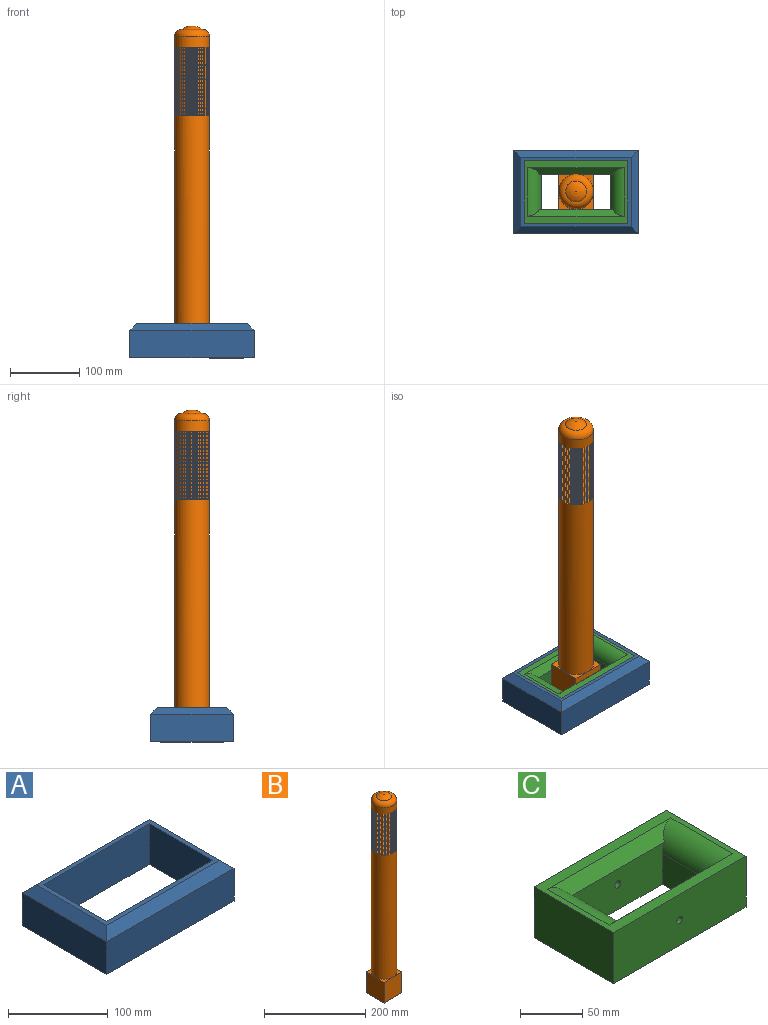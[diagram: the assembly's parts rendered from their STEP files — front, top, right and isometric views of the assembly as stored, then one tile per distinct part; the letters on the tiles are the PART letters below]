
ASSEMBLY  parts=3 mates=2
PART A: 14 faces, bbox 180x120x50 mm
  f0: plane 150x50mm, normal (0,-1,0), area 7500mm2, adj f1,f7,f8,f13
  f1: plane 90x50mm, normal (-1,0,0), area 4500mm2, adj f0,f2,f8,f13
  f2: plane 150x50mm, normal (0,1,0), area 7500mm2, adj f1,f7,f8,f13
  f3: plane 120x40mm, normal (1,0,0), area 4800mm2, adj f4,f6,f10,f13
  f4: plane 180x40mm, normal (0,1,0), area 7200mm2, adj f3,f5,f9,f13
  f5: plane 120x40mm, normal (-1,0,0), area 4800mm2, adj f4,f6,f11,f13
  f6: plane 180x40mm, normal (0,-1,0), area 7200mm2, adj f3,f5,f12,f13
  f7: plane 90x50mm, normal (1,0,0), area 4500mm2, adj f0,f2,f8,f13
  f8: plane 160x100mm, normal (0,0,1), area 2500mm2, adj f0,f1,f2,f7,f9,f10,f11,f12
  f9: plane 180x10mm, normal (0,0.71,0.71), area 2404.2mm2, adj f4,f8,f10,f11
  f10: plane 120x10mm, normal (0.71,0,0.71), area 1555.6mm2, adj f3,f8,f9,f12
  f11: plane 120x10mm, normal (-0.71,0,0.71), area 1555.6mm2, adj f5,f8,f9,f12
  f12: plane 180x10mm, normal (0,-0.71,0.71), area 2404.2mm2, adj f6,f8,f10,f11
  f13: plane 180x120mm, normal (0,0,-1), area 8100mm2, adj f0,f1,f2,f3,f4,f5,f6,f7
PART B: 213 faces, bbox 54.1x54.1x480 mm
  f0: cylinder r=25mm len=300mm, axis (0,0,-1), area 47123.9mm2, adj f1,f204,f205,f206,f212
  f1: plane 50x50mm, normal (0,0,1), area 373.1mm2, adj f0,f2
  f2: cylinder r=22.5mm len=45mm, axis (0,0,-1), area 141.4mm2, adj f1,f5
  f3: cylinder r=25mm len=50mm, axis (0,0,-1), area 157.1mm2, adj f4,f5
  f4: plane 50x50mm, normal (0,0,1), area 373.1mm2, adj f3,f10
  f5: plane 50x50mm, normal (0,0,-1), area 373.1mm2, adj f2,f3
  f6: cylinder r=22.5mm len=45mm, axis (0,0,-1), area 141.4mm2, adj f9,f12
  f7: cylinder r=25mm len=50mm, axis (0,0,-1), area 157.1mm2, adj f8,f9
  f8: plane 50x50mm, normal (0,0,1), area 373.1mm2, adj f7,f14
  f9: plane 50x50mm, normal (0,0,-1), area 373.1mm2, adj f6,f7
  f10: cylinder r=22.5mm len=45mm, axis (0,0,-1), area 141.4mm2, adj f4,f13
  f11: cylinder r=25mm len=50mm, axis (0,0,-1), area 157.1mm2, adj f12,f13
  f12: plane 50x50mm, normal (0,0,1), area 373.1mm2, adj f6,f11
  f13: plane 50x50mm, normal (0,0,-1), area 373.1mm2, adj f10,f11
  f14: cylinder r=22.5mm len=45mm, axis (0,0,-1), area 141.4mm2, adj f8,f17
  f15: cylinder r=25mm len=50mm, axis (0,0,-1), area 157.1mm2, adj f16,f17
  f16: plane 50x50mm, normal (0,0,1), area 373.1mm2, adj f15,f18
  f17: plane 50x50mm, normal (0,0,-1), area 373.1mm2, adj f14,f15
  f18: cylinder r=22.5mm len=45mm, axis (0,0,-1), area 141.4mm2, adj f16,f21
  f19: cylinder r=25mm len=50mm, axis (0,0,-1), area 157.1mm2, adj f20,f21
  f20: plane 50x50mm, normal (0,0,1), area 373.1mm2, adj f19,f22
  f21: plane 50x50mm, normal (0,0,-1), area 373.1mm2, adj f18,f19
  f22: cylinder r=22.5mm len=45mm, axis (0,0,-1), area 141.4mm2, adj f20,f25
  f23: cylinder r=25mm len=50mm, axis (0,0,-1), area 157.1mm2, adj f24,f25
  f24: plane 50x50mm, normal (0,0,1), area 373.1mm2, adj f23,f26
  f25: plane 50x50mm, normal (0,0,-1), area 373.1mm2, adj f22,f23
  f26: cylinder r=22.5mm len=45mm, axis (0,0,-1), area 141.4mm2, adj f24,f29
  f27: cylinder r=25mm len=50mm, axis (0,0,-1), area 157.1mm2, adj f28,f29
  f28: plane 50x50mm, normal (0,0,1), area 373.1mm2, adj f27,f30
  f29: plane 50x50mm, normal (0,0,-1), area 373.1mm2, adj f26,f27
  f30: cylinder r=22.5mm len=45mm, axis (0,0,-1), area 141.4mm2, adj f28,f33
  f31: cylinder r=25mm len=50mm, axis (0,0,-1), area 157.1mm2, adj f32,f33
  f32: plane 50x50mm, normal (0,0,1), area 373.1mm2, adj f31,f34
  f33: plane 50x50mm, normal (0,0,-1), area 373.1mm2, adj f30,f31
  f34: cylinder r=22.5mm len=45mm, axis (0,0,-1), area 141.4mm2, adj f32,f37
  f35: cylinder r=25mm len=50mm, axis (0,0,-1), area 157.1mm2, adj f36,f37
  f36: plane 50x50mm, normal (0,0,1), area 373.1mm2, adj f35,f38
  f37: plane 50x50mm, normal (0,0,-1), area 373.1mm2, adj f34,f35
  f38: cylinder r=22.5mm len=45mm, axis (0,0,-1), area 141.4mm2, adj f36,f41
  f39: cylinder r=25mm len=50mm, axis (0,0,-1), area 157.1mm2, adj f40,f41
  f40: plane 50x50mm, normal (0,0,1), area 373.1mm2, adj f39,f42
  f41: plane 50x50mm, normal (0,0,-1), area 373.1mm2, adj f38,f39
  f42: cylinder r=22.5mm len=45mm, axis (0,0,-1), area 141.4mm2, adj f40,f45
  f43: cylinder r=25mm len=50mm, axis (0,0,-1), area 157.1mm2, adj f44,f45
  f44: plane 50x50mm, normal (0,0,1), area 373.1mm2, adj f43,f46
  f45: plane 50x50mm, normal (0,0,-1), area 373.1mm2, adj f42,f43
  f46: cylinder r=22.5mm len=45mm, axis (0,0,-1), area 141.4mm2, adj f44,f49
  f47: cylinder r=25mm len=50mm, axis (0,0,-1), area 157.1mm2, adj f48,f49
  f48: plane 50x50mm, normal (0,0,1), area 373.1mm2, adj f47,f50
  f49: plane 50x50mm, normal (0,0,-1), area 373.1mm2, adj f46,f47
  f50: cylinder r=22.5mm len=45mm, axis (0,0,-1), area 141.4mm2, adj f48,f53
  f51: cylinder r=25mm len=50mm, axis (0,0,-1), area 157.1mm2, adj f52,f53
  f52: plane 50x50mm, normal (0,0,1), area 373.1mm2, adj f51,f54
  f53: plane 50x50mm, normal (0,0,-1), area 373.1mm2, adj f50,f51
  f54: cylinder r=22.5mm len=45mm, axis (0,0,-1), area 141.4mm2, adj f52,f57
  f55: cylinder r=25mm len=50mm, axis (0,0,-1), area 157.1mm2, adj f56,f57
  f56: plane 50x50mm, normal (0,0,1), area 373.1mm2, adj f55,f58
  f57: plane 50x50mm, normal (0,0,-1), area 373.1mm2, adj f54,f55
  f58: cylinder r=22.5mm len=45mm, axis (0,0,-1), area 141.4mm2, adj f56,f61
  f59: cylinder r=25mm len=50mm, axis (0,0,-1), area 157.1mm2, adj f60,f61
  f60: plane 50x50mm, normal (0,0,1), area 373.1mm2, adj f59,f62
  f61: plane 50x50mm, normal (0,0,-1), area 373.1mm2, adj f58,f59
  f62: cylinder r=22.5mm len=45mm, axis (0,0,-1), area 141.4mm2, adj f60,f65
  f63: cylinder r=25mm len=50mm, axis (0,0,-1), area 157.1mm2, adj f64,f65
  f64: plane 50x50mm, normal (0,0,1), area 373.1mm2, adj f63,f66
  f65: plane 50x50mm, normal (0,0,-1), area 373.1mm2, adj f62,f63
  f66: cylinder r=22.5mm len=45mm, axis (0,0,-1), area 141.4mm2, adj f64,f69
  f67: cylinder r=25mm len=50mm, axis (0,0,-1), area 157.1mm2, adj f68,f69
  f68: plane 50x50mm, normal (0,0,1), area 373.1mm2, adj f67,f70
  f69: plane 50x50mm, normal (0,0,-1), area 373.1mm2, adj f66,f67
  f70: cylinder r=22.5mm len=45mm, axis (0,0,-1), area 141.4mm2, adj f68,f73
  f71: cylinder r=25mm len=50mm, axis (0,0,-1), area 157.1mm2, adj f72,f73
  f72: plane 50x50mm, normal (0,0,1), area 373.1mm2, adj f71,f74
  f73: plane 50x50mm, normal (0,0,-1), area 373.1mm2, adj f70,f71
  f74: cylinder r=22.5mm len=45mm, axis (0,0,-1), area 141.4mm2, adj f72,f77
  f75: cylinder r=25mm len=50mm, axis (0,0,-1), area 157.1mm2, adj f76,f77
  f76: plane 50x50mm, normal (0,0,1), area 373.1mm2, adj f75,f78
  f77: plane 50x50mm, normal (0,0,-1), area 373.1mm2, adj f74,f75
  f78: cylinder r=22.5mm len=45mm, axis (0,0,-1), area 141.4mm2, adj f76,f81
  f79: cylinder r=25mm len=50mm, axis (0,0,-1), area 157.1mm2, adj f80,f81
  f80: plane 50x50mm, normal (0,0,1), area 373.1mm2, adj f79,f82
  f81: plane 50x50mm, normal (0,0,-1), area 373.1mm2, adj f78,f79
  f82: cylinder r=22.5mm len=45mm, axis (0,0,-1), area 141.4mm2, adj f80,f85
  f83: cylinder r=25mm len=50mm, axis (0,0,-1), area 157.1mm2, adj f84,f85
  f84: plane 50x50mm, normal (0,0,1), area 373.1mm2, adj f83,f86
  f85: plane 50x50mm, normal (0,0,-1), area 373.1mm2, adj f82,f83
  f86: cylinder r=22.5mm len=45mm, axis (0,0,-1), area 141.4mm2, adj f84,f89
  f87: cylinder r=25mm len=50mm, axis (0,0,-1), area 157.1mm2, adj f88,f89
  f88: plane 50x50mm, normal (0,0,1), area 373.1mm2, adj f87,f90
  f89: plane 50x50mm, normal (0,0,-1), area 373.1mm2, adj f86,f87
  f90: cylinder r=22.5mm len=45mm, axis (0,0,-1), area 141.4mm2, adj f88,f93
  f91: cylinder r=25mm len=50mm, axis (0,0,-1), area 157.1mm2, adj f92,f93
  f92: plane 50x50mm, normal (0,0,1), area 373.1mm2, adj f91,f94
  f93: plane 50x50mm, normal (0,0,-1), area 373.1mm2, adj f90,f91
  f94: cylinder r=22.5mm len=45mm, axis (0,0,-1), area 141.4mm2, adj f92,f97
  f95: cylinder r=25mm len=50mm, axis (0,0,-1), area 157.1mm2, adj f96,f97
  f96: plane 50x50mm, normal (0,0,1), area 373.1mm2, adj f95,f98
  f97: plane 50x50mm, normal (0,0,-1), area 373.1mm2, adj f94,f95
  f98: cylinder r=22.5mm len=45mm, axis (0,0,-1), area 141.4mm2, adj f96,f101
  f99: cylinder r=25mm len=50mm, axis (0,0,-1), area 157.1mm2, adj f100,f101
  f100: plane 50x50mm, normal (0,0,1), area 373.1mm2, adj f99,f102
  f101: plane 50x50mm, normal (0,0,-1), area 373.1mm2, adj f98,f99
  f102: cylinder r=22.5mm len=45mm, axis (0,0,-1), area 141.4mm2, adj f100,f105
  f103: cylinder r=25mm len=50mm, axis (0,0,-1), area 157.1mm2, adj f104,f105
  f104: plane 50x50mm, normal (0,0,1), area 373.1mm2, adj f103,f106
  f105: plane 50x50mm, normal (0,0,-1), area 373.1mm2, adj f102,f103
  f106: cylinder r=22.5mm len=45mm, axis (0,0,-1), area 141.4mm2, adj f104,f109
  f107: cylinder r=25mm len=50mm, axis (0,0,-1), area 157.1mm2, adj f108,f109
  f108: plane 50x50mm, normal (0,0,1), area 373.1mm2, adj f107,f110
  f109: plane 50x50mm, normal (0,0,-1), area 373.1mm2, adj f106,f107
  f110: cylinder r=22.5mm len=45mm, axis (0,0,-1), area 141.4mm2, adj f108,f113
  f111: cylinder r=25mm len=50mm, axis (0,0,-1), area 157.1mm2, adj f112,f113
  f112: plane 50x50mm, normal (0,0,1), area 373.1mm2, adj f111,f114
  f113: plane 50x50mm, normal (0,0,-1), area 373.1mm2, adj f110,f111
  f114: cylinder r=22.5mm len=45mm, axis (0,0,-1), area 141.4mm2, adj f112,f117
  f115: cylinder r=25mm len=50mm, axis (0,0,-1), area 157.1mm2, adj f116,f117
  f116: plane 50x50mm, normal (0,0,1), area 373.1mm2, adj f115,f118
  f117: plane 50x50mm, normal (0,0,-1), area 373.1mm2, adj f114,f115
  f118: cylinder r=22.5mm len=45mm, axis (0,0,-1), area 141.4mm2, adj f116,f121
  f119: cylinder r=25mm len=50mm, axis (0,0,-1), area 157.1mm2, adj f120,f121
  f120: plane 50x50mm, normal (0,0,1), area 373.1mm2, adj f119,f122
  f121: plane 50x50mm, normal (0,0,-1), area 373.1mm2, adj f118,f119
  f122: cylinder r=22.5mm len=45mm, axis (0,0,-1), area 141.4mm2, adj f120,f125
  f123: cylinder r=25mm len=50mm, axis (0,0,-1), area 157.1mm2, adj f124,f125
  f124: plane 50x50mm, normal (0,0,1), area 373.1mm2, adj f123,f126
  f125: plane 50x50mm, normal (0,0,-1), area 373.1mm2, adj f122,f123
  f126: cylinder r=22.5mm len=45mm, axis (0,0,-1), area 141.4mm2, adj f124,f129
  f127: cylinder r=25mm len=50mm, axis (0,0,-1), area 157.1mm2, adj f128,f129
  f128: plane 50x50mm, normal (0,0,1), area 373.1mm2, adj f127,f130
  f129: plane 50x50mm, normal (0,0,-1), area 373.1mm2, adj f126,f127
  f130: cylinder r=22.5mm len=45mm, axis (0,0,-1), area 141.4mm2, adj f128,f133
  f131: cylinder r=25mm len=50mm, axis (0,0,-1), area 157.1mm2, adj f132,f133
  f132: plane 50x50mm, normal (0,0,1), area 373.1mm2, adj f131,f134
  f133: plane 50x50mm, normal (0,0,-1), area 373.1mm2, adj f130,f131
  f134: cylinder r=22.5mm len=45mm, axis (0,0,-1), area 141.4mm2, adj f132,f137
  f135: cylinder r=25mm len=50mm, axis (0,0,-1), area 157.1mm2, adj f136,f137
  f136: plane 50x50mm, normal (0,0,1), area 373.1mm2, adj f135,f138
  f137: plane 50x50mm, normal (0,0,-1), area 373.1mm2, adj f134,f135
  f138: cylinder r=22.5mm len=45mm, axis (0,0,-1), area 141.4mm2, adj f136,f141
  f139: cylinder r=25mm len=50mm, axis (0,0,-1), area 157.1mm2, adj f140,f141
  f140: plane 50x50mm, normal (0,0,1), area 373.1mm2, adj f139,f142
  f141: plane 50x50mm, normal (0,0,-1), area 373.1mm2, adj f138,f139
  f142: cylinder r=22.5mm len=45mm, axis (0,0,-1), area 141.4mm2, adj f140,f145
  f143: cylinder r=25mm len=50mm, axis (0,0,-1), area 157.1mm2, adj f144,f145
  f144: plane 50x50mm, normal (0,0,1), area 373.1mm2, adj f143,f146
  f145: plane 50x50mm, normal (0,0,-1), area 373.1mm2, adj f142,f143
  f146: cylinder r=22.5mm len=45mm, axis (0,0,-1), area 141.4mm2, adj f144,f149
  f147: cylinder r=25mm len=50mm, axis (0,0,-1), area 157.1mm2, adj f148,f149
  f148: plane 50x50mm, normal (0,0,1), area 373.1mm2, adj f147,f150
  f149: plane 50x50mm, normal (0,0,-1), area 373.1mm2, adj f146,f147
  f150: cylinder r=22.5mm len=45mm, axis (0,0,-1), area 141.4mm2, adj f148,f153
  f151: cylinder r=25mm len=50mm, axis (0,0,-1), area 157.1mm2, adj f152,f153
  f152: plane 50x50mm, normal (0,0,1), area 373.1mm2, adj f151,f154
  f153: plane 50x50mm, normal (0,0,-1), area 373.1mm2, adj f150,f151
  f154: cylinder r=22.5mm len=45mm, axis (0,0,-1), area 141.4mm2, adj f152,f157
  f155: cylinder r=25mm len=50mm, axis (0,0,-1), area 157.1mm2, adj f156,f157
  f156: plane 50x50mm, normal (0,0,1), area 373.1mm2, adj f155,f158
  f157: plane 50x50mm, normal (0,0,-1), area 373.1mm2, adj f154,f155
  f158: cylinder r=22.5mm len=45mm, axis (0,0,-1), area 141.4mm2, adj f156,f161
  f159: cylinder r=25mm len=50mm, axis (0,0,-1), area 157.1mm2, adj f160,f161
  f160: plane 50x50mm, normal (0,0,1), area 373.1mm2, adj f159,f162
  f161: plane 50x50mm, normal (0,0,-1), area 373.1mm2, adj f158,f159
  f162: cylinder r=22.5mm len=45mm, axis (0,0,-1), area 141.4mm2, adj f160,f165
  f163: cylinder r=25mm len=50mm, axis (0,0,-1), area 157.1mm2, adj f164,f165
  f164: plane 50x50mm, normal (0,0,1), area 373.1mm2, adj f163,f166
  f165: plane 50x50mm, normal (0,0,-1), area 373.1mm2, adj f162,f163
  f166: cylinder r=22.5mm len=45mm, axis (0,0,-1), area 141.4mm2, adj f164,f169
  f167: cylinder r=25mm len=50mm, axis (0,0,-1), area 157.1mm2, adj f168,f169
  f168: plane 50x50mm, normal (0,0,1), area 373.1mm2, adj f167,f170
  f169: plane 50x50mm, normal (0,0,-1), area 373.1mm2, adj f166,f167
  f170: cylinder r=22.5mm len=45mm, axis (0,0,-1), area 141.4mm2, adj f168,f173
  f171: cylinder r=25mm len=50mm, axis (0,0,-1), area 157.1mm2, adj f172,f173
  f172: plane 50x50mm, normal (0,0,1), area 373.1mm2, adj f171,f174
  f173: plane 50x50mm, normal (0,0,-1), area 373.1mm2, adj f170,f171
  f174: cylinder r=22.5mm len=45mm, axis (0,0,-1), area 141.4mm2, adj f172,f177
  f175: cylinder r=25mm len=50mm, axis (0,0,-1), area 157.1mm2, adj f176,f177
  f176: plane 50x50mm, normal (0,0,1), area 373.1mm2, adj f175,f178
  f177: plane 50x50mm, normal (0,0,-1), area 373.1mm2, adj f174,f175
  f178: cylinder r=22.5mm len=45mm, axis (0,0,-1), area 141.4mm2, adj f176,f181
  f179: cylinder r=25mm len=50mm, axis (0,0,-1), area 157.1mm2, adj f180,f181
  f180: plane 50x50mm, normal (0,0,1), area 373.1mm2, adj f179,f182
  f181: plane 50x50mm, normal (0,0,-1), area 373.1mm2, adj f178,f179
  f182: cylinder r=22.5mm len=45mm, axis (0,0,-1), area 141.4mm2, adj f180,f185
  f183: cylinder r=25mm len=50mm, axis (0,0,-1), area 157.1mm2, adj f184,f185
  f184: plane 50x50mm, normal (0,0,1), area 373.1mm2, adj f183,f186
  f185: plane 50x50mm, normal (0,0,-1), area 373.1mm2, adj f182,f183
  f186: cylinder r=22.5mm len=45mm, axis (0,0,-1), area 141.4mm2, adj f184,f189
  f187: cylinder r=25mm len=50mm, axis (0,0,-1), area 157.1mm2, adj f188,f189
  f188: plane 50x50mm, normal (0,0,1), area 373.1mm2, adj f187,f190
  f189: plane 50x50mm, normal (0,0,-1), area 373.1mm2, adj f186,f187
  f190: cylinder r=22.5mm len=45mm, axis (0,0,-1), area 141.4mm2, adj f188,f193
  f191: cylinder r=25mm len=50mm, axis (0,0,-1), area 157.1mm2, adj f192,f193
  f192: plane 50x50mm, normal (0,0,1), area 373.1mm2, adj f191,f194
  f193: plane 50x50mm, normal (0,0,-1), area 373.1mm2, adj f190,f191
  f194: cylinder r=22.5mm len=45mm, axis (0,0,-1), area 141.4mm2, adj f192,f197
  f195: cylinder r=25mm len=50mm, axis (0,0,-1), area 157.1mm2, adj f196,f197
  f196: plane 50x50mm, normal (0,0,1), area 373.1mm2, adj f195,f198
  f197: plane 50x50mm, normal (0,0,-1), area 373.1mm2, adj f194,f195
  f198: cylinder r=22.5mm len=45mm, axis (0,0,-1), area 141.4mm2, adj f196,f200
  f199: cylinder r=25mm len=50mm, axis (0,0,-1), area 2513.3mm2, adj f200,f201
  f200: plane 50x50mm, normal (0,0,-1), area 373.1mm2, adj f198,f199
  f201: torus R=15mm, axis (0,0,1), area 2108.8mm2, adj f199,f203
  f202: plane 0.67x0.67mm, normal (0,0,1), area 0.4mm2, adj f203
  f203: torus R=0.34mm, axis (0,0,-1), area 787.4mm2, adj f201,f202
  f204: plane 25x25mm, normal (0,0,1), area 134.1mm2, adj f0,f207,f208
  f205: plane 25x25mm, normal (0,0,1), area 134.1mm2, adj f0,f207,f210
  f206: plane 25x25mm, normal (0,0,1), area 134.1mm2, adj f0,f209,f210
  f207: plane 50x50mm, normal (0,1,0), area 2500mm2, adj f204,f205,f208,f210,f211
  f208: plane 50x50mm, normal (1,0,0), area 2500mm2, adj f204,f207,f209,f211,f212
  f209: plane 50x50mm, normal (0,-1,0), area 2500mm2, adj f206,f208,f210,f211,f212
  f210: plane 50x50mm, normal (-1,0,0), area 2500mm2, adj f205,f206,f207,f209,f211
  f211: plane 50x50mm, normal (0,0,-1), area 2500mm2, adj f207,f208,f209,f210
  f212: plane 25x25mm, normal (0,0,1), area 134.1mm2, adj f0,f208,f209
PART C: 16 faces, bbox 150x90x50 mm
  f0: plane 90x50mm, normal (1,0,0), area 4500mm2, adj f1,f7,f8,f9
  f1: plane 150x50mm, normal (0,1,0), area 7464.1mm2, adj f0,f2,f8,f9,f15
  f2: plane 90x50mm, normal (-1,0,0), area 4500mm2, adj f1,f7,f8,f9
  f3: plane 50x30mm, normal (-1,0,0), area 1500mm2, adj f4,f6,f9,f11
  f4: plane 105.36x40mm, normal (0,1,0), area 3981.5mm2, adj f3,f5,f9,f10,f11,f13,f14
  f5: plane 50x30mm, normal (1,0,0), area 1500mm2, adj f4,f6,f9,f10
  f6: plane 105.36x40mm, normal (0,-1,0), area 3981.5mm2, adj f3,f5,f9,f10,f11,f12,f15
  f7: plane 150x50mm, normal (0,-1,0), area 7464.1mm2, adj f0,f2,f8,f9,f14
  f8: plane 150x90mm, normal (0,0,1), area 3700mm2, adj f0,f1,f2,f7,f10,f11,f12,f13
  f9: plane 150x90mm, normal (0,0,-1), area 8500mm2, adj f0,f1,f2,f3,f4,f5,f6,f7
  f10: cylinder r=20mm len=70mm, axis (0,-1,0), area 1844.7mm2, adj f4,f5,f6,f8,f12,f13
  f11: cylinder r=20mm len=70mm, axis (0,1,0), area 1844.7mm2, adj f3,f4,f6,f8,f12,f13
  f12: plane 140x10mm, normal (0,-0.71,0.71), area 1632.5mm2, adj f6,f8,f10,f11
  f13: plane 140x10mm, normal (0,0.71,0.71), area 1632.5mm2, adj f4,f8,f10,f11
  f14: cylinder r=3.38mm len=20mm, axis (0,-1,0), area 424.5mm2, adj f4,f7
  f15: cylinder r=3.38mm len=20mm, axis (0,-1,0), area 424.5mm2, adj f1,f6
PLACE A t=(-38.6,117.81,-4.85)mm fixed
PLACE B t=(-19.16,104.08,20.15)mm
PLACE C t=(-63.48,129.67,-29.85)mm
MATE revolute C.f14 <-> B.f207  axis (0,-1,0) through (-38.6,142.81,-4.85)mm
MATE fastened A.f0 <-> C.f14  axis (0,-1,0) through (-38.6,162.81,-4.85)mm
